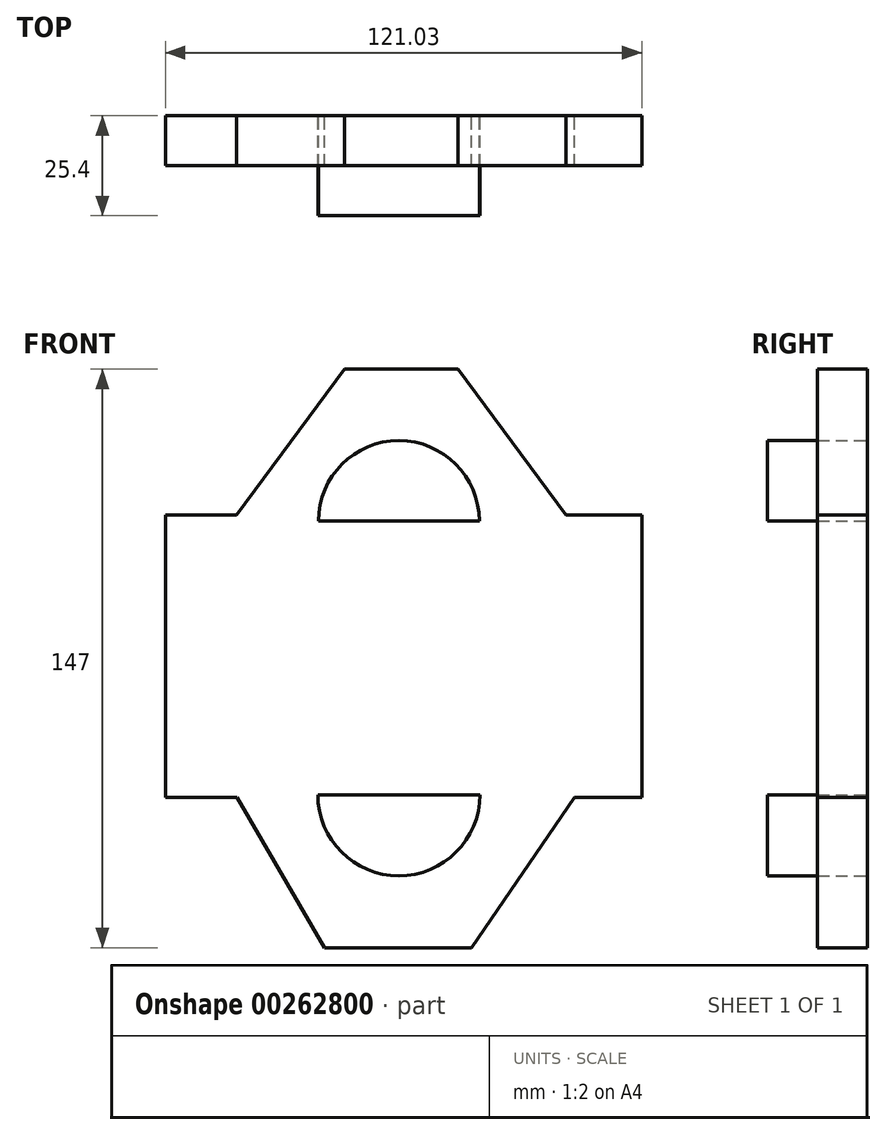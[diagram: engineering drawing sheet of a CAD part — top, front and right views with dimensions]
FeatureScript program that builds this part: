
annotation { "Feature Type Name" : "Feature", "Feature Type Description" : "" }
export const myFeature = defineFeature(function(context is Context, id is Id, definition is map)
    precondition{}
    {
        {
            var Q0;
            Q0=qCreatedBy(makeId("Front.planeOp"),FACE);
            var sketch = newSketch(context, id + "F0", { "sketchPlane" : qUnion([Q0])});
            skArc(sketch, "E0", {"start": v(-20.6, -32.42) * mm, "mid": v(0, -53.02) * mm, "end": v(20.6, -32.42) * mm});
            skArc(sketch, "E1", {"start": v(20.42, 37.14) * mm, "mid": v(0, 57.56) * mm, "end": v(-20.42, 37.14) * mm});
            skLineSegment(sketch, "E2", {"start": v(20.6, -32.42) * mm, "end": v(-20.6, -32.42) * mm});
            skLineSegment(sketch, "E3", {"start": v(20.42, 37.14) * mm, "end": v(-20.42, 37.14) * mm});
            skLineSegment(sketch, "E4.bottom", {"start": v(37.42, 37.14) * mm, "end": v(32.41, 37.14) * mm});
            skLineSegment(sketch, "E4.left", {"start": v(43.77, 30.79) * mm, "end": v(43.77, -26.07) * mm});
            skLineSegment(sketch, "E4.right", {"start": v(-45.86, 30.79) * mm, "end": v(-45.86, -26.07) * mm});
            skLineSegment(sketch, "E5", {"start": v(-35.26, 25.12) * mm, "end": v(-11.23, 25.12) * mm});
            skLineSegment(sketch, "E6", {"start": v(31.75, 25.26) * mm, "end": v(9.84, 25.26) * mm});
            skLineSegment(sketch, "E7", {"start": v(-34.84, -21.1) * mm, "end": v(-10.52, -21.1) * mm});
            skLineSegment(sketch, "E8", {"start": v(30.9, -21.67) * mm, "end": v(8.99, -21.67) * mm});
            skArc(sketch, "E9.0.startCap", {"start": v(-35.26, 18.77) * mm, "mid": v(-41.61, 25.12) * mm, "end": v(-35.26, 31.47) * mm});
            skArc(sketch, "E9.0.endCap", {"start": v(-11.23, 31.47) * mm, "mid": v(-4.88, 25.12) * mm, "end": v(-11.23, 18.77) * mm});
            skLineSegment(sketch, "E9.0.left", {"start": v(-35.26, 31.47) * mm, "end": v(-11.23, 31.47) * mm});
            skLineSegment(sketch, "E9.0.right", {"start": v(-35.26, 18.77) * mm, "end": v(-11.23, 18.77) * mm});
            skArc(sketch, "E9.1.startCap", {"start": v(31.75, 31.61) * mm, "mid": v(38.1, 25.26) * mm, "end": v(31.75, 18.91) * mm});
            skArc(sketch, "E9.1.endCap", {"start": v(9.84, 18.91) * mm, "mid": v(3.49, 25.26) * mm, "end": v(9.84, 31.61) * mm});
            skLineSegment(sketch, "E9.1.left", {"start": v(31.75, 18.91) * mm, "end": v(9.84, 18.91) * mm});
            skLineSegment(sketch, "E9.1.right", {"start": v(31.75, 31.61) * mm, "end": v(9.84, 31.61) * mm});
            skArc(sketch, "E9.2.startCap", {"start": v(-34.84, -27.46) * mm, "mid": v(-41.19, -21.1) * mm, "end": v(-34.84, -14.76) * mm});
            skArc(sketch, "E9.2.endCap", {"start": v(-10.52, -14.76) * mm, "mid": v(-4.17, -21.1) * mm, "end": v(-10.52, -27.46) * mm});
            skLineSegment(sketch, "E9.2.left", {"start": v(-34.84, -14.76) * mm, "end": v(-10.52, -14.76) * mm});
            skLineSegment(sketch, "E9.2.right", {"start": v(-34.84, -27.46) * mm, "end": v(-10.52, -27.46) * mm});
            skArc(sketch, "E9.3.startCap", {"start": v(30.9, -15.32) * mm, "mid": v(37.25, -21.67) * mm, "end": v(30.9, -28.02) * mm});
            skArc(sketch, "E9.3.endCap", {"start": v(8.99, -28.02) * mm, "mid": v(2.64, -21.67) * mm, "end": v(8.99, -15.32) * mm});
            skLineSegment(sketch, "E9.3.left", {"start": v(30.9, -28.02) * mm, "end": v(8.99, -28.02) * mm});
            skLineSegment(sketch, "E9.3.right", {"start": v(30.9, -15.32) * mm, "end": v(8.99, -15.32) * mm});
            skPoint(sketch, "E10.visualSharp", {"position": v(-45.86, 37.14) * mm});
            skArc(sketch, "E10.filletArc", {"start": v(-39.51, 37.14) * mm, "mid": v(-44, 35.28) * mm, "end": v(-45.86, 30.79) * mm});
            skPoint(sketch, "E11.visualSharp", {"position": v(43.77, 37.14) * mm});
            skArc(sketch, "E11.filletArc", {"start": v(43.77, 30.79) * mm, "mid": v(41.9, 35.28) * mm, "end": v(37.42, 37.14) * mm});
            skPoint(sketch, "E12.visualSharp", {"position": v(43.77, -32.42) * mm});
            skArc(sketch, "E12.filletArc", {"start": v(37.42, -32.42) * mm, "mid": v(41.9, -30.56) * mm, "end": v(43.77, -26.07) * mm});
            skPoint(sketch, "E13.visualSharp", {"position": v(-45.86, -32.42) * mm});
            skArc(sketch, "E13.filletArc", {"start": v(-45.86, -26.07) * mm, "mid": v(-44, -30.56) * mm, "end": v(-39.51, -32.42) * mm});
            skLineSegment(sketch, "E14", {"start": v(-21.12, 76.44) * mm, "end": v(21.43, 76.3) * mm});
            skLineSegment(sketch, "E15", {"start": v(21.43, 76.3) * mm, "end": v(32.41, 37.14) * mm});
            skLineSegment(sketch, "E16", {"start": v(-20.86, 76.57) * mm, "end": v(-31.77, 37.14) * mm});
            skLineSegment(sketch, "E17.trimOffspring", {"start": v(-31.77, 37.14) * mm, "end": v(-39.51, 37.14) * mm});
            skLineSegment(sketch, "E18", {"start": v(-20.6, -70.85) * mm, "end": v(22.81, -70.85) * mm});
            skLineSegment(sketch, "E19", {"start": v(-20.6, -71) * mm, "end": v(-35.29, -32.53) * mm});
            skLineSegment(sketch, "E20", {"start": v(22.5, -70.23) * mm, "end": v(37.42, -32.42) * mm});
            skLineSegment(sketch, "E21", {"start": v(-39.51, -32.42) * mm, "end": v(-35.29, -32.53) * mm});
            skSolve(sketch);
        }
        {
            var Q0;
            Q0=makeQuery(id+"F0.imprint","IMPRINT",FACE,{"disambiguationData":[TD([[makeQuery(id+"F0.imprint","IMPRINT",EDGE,{"derivedFrom":sQuery(id+"F0.wireOp",EDGE,"E9.0.startCap")}),-1.0]])]});
            var Q1;
            Q1=makeQuery(id+"F0.imprint","IMPRINT",FACE,{"disambiguationData":[TD([[makeQuery(id+"F0.imprint","IMPRINT",EDGE,{"derivedFrom":sQuery(id+"F0.wireOp",EDGE,"E1")}),1.0]])]});
            var Q2;
            Q2=makeQuery(id+"F0.imprint","IMPRINT",FACE,{"disambiguationData":[TD([[makeQuery(id+"F0.imprint","IMPRINT",EDGE,{"derivedFrom":sQuery(id+"F0.wireOp",EDGE,"E9.1.startCap")}),-1.0]])]});
            var Q3;
            Q3=makeQuery(id+"F0.imprint","IMPRINT",FACE,{"disambiguationData":[TD([[makeQuery(id+"F0.imprint","IMPRINT",EDGE,{"derivedFrom":sQuery(id+"F0.wireOp",EDGE,"E9.2.startCap")}),-1.0]])]});
            var Q4;
            Q4=makeQuery(id+"F0.imprint","IMPRINT",FACE,{"disambiguationData":[TD([[makeQuery(id+"F0.imprint","IMPRINT",EDGE,{"derivedFrom":sQuery(id+"F0.wireOp",EDGE,"E0")}),1.0]])]});
            var Q5;
            Q5=makeQuery(id+"F0.imprint","IMPRINT",FACE,{"disambiguationData":[TD([[makeQuery(id+"F0.imprint","IMPRINT",EDGE,{"derivedFrom":sQuery(id+"F0.wireOp",EDGE,"E9.3.startCap")}),-1.0]])]});
            extrude(context, id + "F1", {"entities" : qUnion([Q0, Q1, Q2, Q3, Q4, Q5]), "depth" : 25.4 * mm});
        }
        {
            var Q0;
            Q0=qCreatedBy(makeId("Front.planeOp"),FACE);
            var sketch = newSketch(context, id + "F2", { "sketchPlane" : qUnion([Q0])});
            skLineSegment(sketch, "E22.bottom", {"start": v(61.7, 38.62) * mm, "end": v(-59.34, 38.62) * mm});
            skLineSegment(sketch, "E22.top", {"start": v(61.7, -33.1) * mm, "end": v(-59.34, -33.1) * mm});
            skLineSegment(sketch, "E22.left", {"start": v(61.7, 38.62) * mm, "end": v(61.7, -33.1) * mm});
            skLineSegment(sketch, "E22.right", {"start": v(-59.34, 38.62) * mm, "end": v(-59.34, -33.1) * mm});
            skLineSegment(sketch, "E23", {"start": v(-41.27, 38.62) * mm, "end": v(-13.79, 75.7) * mm});
            skLineSegment(sketch, "E24", {"start": v(-13.79, 75.7) * mm, "end": v(15.01, 75.7) * mm});
            skLineSegment(sketch, "E25", {"start": v(15.01, 75.7) * mm, "end": v(42.5, 38.62) * mm});
            skLineSegment(sketch, "E26", {"start": v(-41.08, -33.1) * mm, "end": v(-18.87, -71.3) * mm});
            skLineSegment(sketch, "E27", {"start": v(-18.87, -71.3) * mm, "end": v(18.4, -71.3) * mm});
            skLineSegment(sketch, "E28", {"start": v(18.4, -71.3) * mm, "end": v(44.56, -33.1) * mm});
            skSolve(sketch);
        }
        {
            var Q0;
            {var subQ0=sQuery(id+"F2.wireOp",EDGE,"E22.left");Q0=makeQuery(id+"F2.imprint","IMPRINT",FACE,{"disambiguationData":[TD([[makeQuery(id+"F2.imprint","IMPRINT",EDGE,{"derivedFrom":subQ0}),-1.0]])]});}
            var Q1;
            {var subQ0=sQuery(id+"F2.wireOp",EDGE,"E23");Q1=makeQuery(id+"F2.imprint","IMPRINT",FACE,{"disambiguationData":[TD([[makeQuery(id+"F2.imprint","IMPRINT",EDGE,{"derivedFrom":subQ0}),-1.0]])]});}
            var Q2;
            {var subQ0=sQuery(id+"F2.wireOp",EDGE,"E26");Q2=makeQuery(id+"F2.imprint","IMPRINT",FACE,{"disambiguationData":[TD([[makeQuery(id+"F2.imprint","IMPRINT",EDGE,{"derivedFrom":subQ0}),1.0]])]});}
            extrude(context, id + "F3", {"entities" : qUnion([Q0, Q1, Q2]), "depth" : 12.7 * mm});
        }
    });
